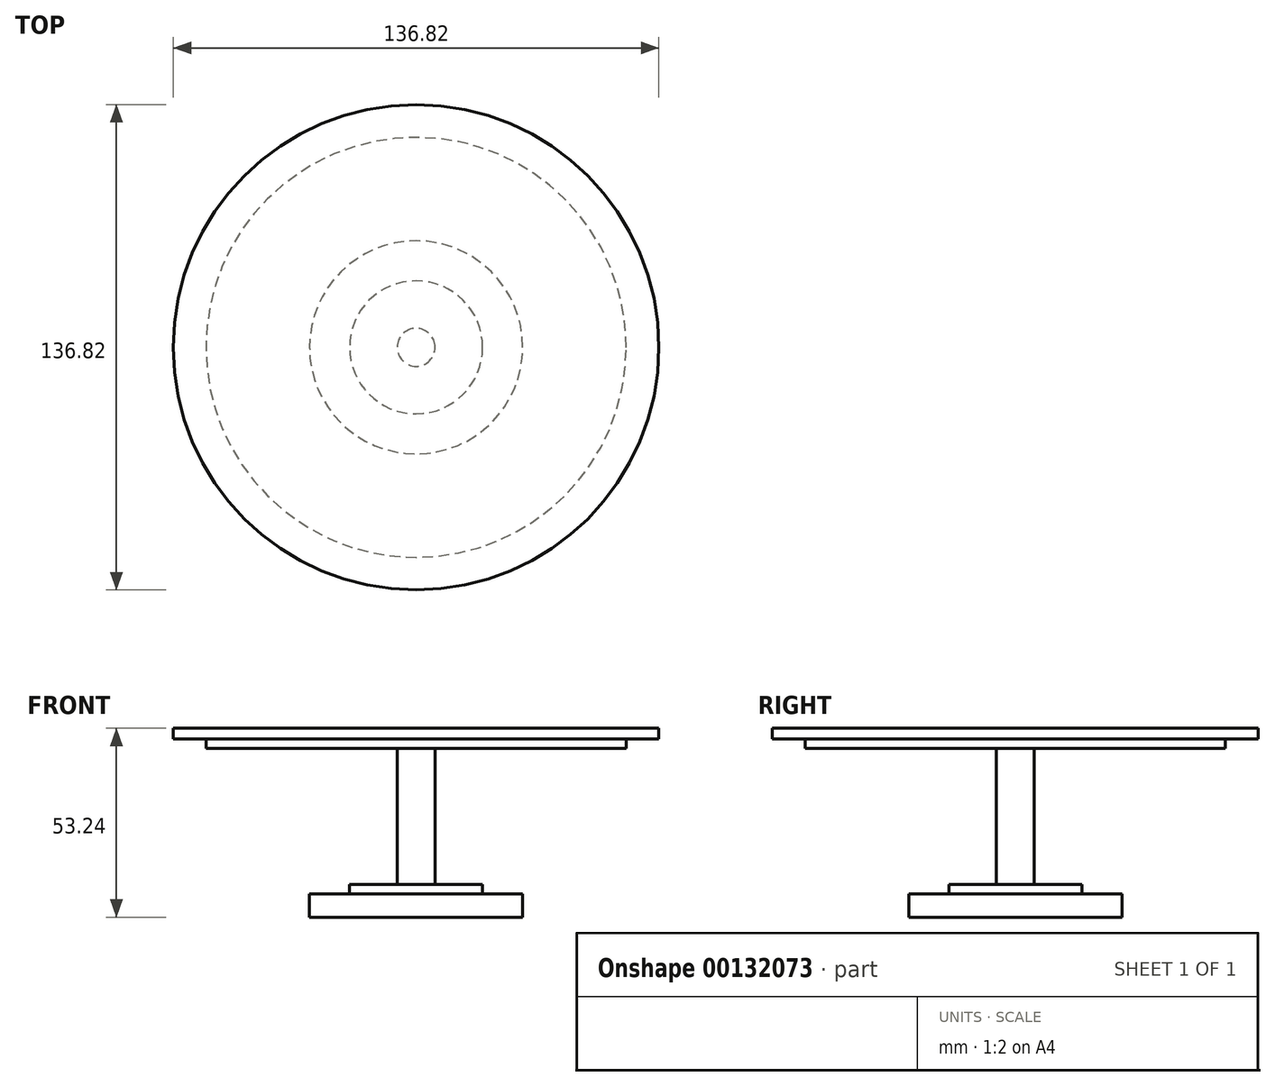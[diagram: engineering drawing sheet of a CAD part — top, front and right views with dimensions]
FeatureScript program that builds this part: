
annotation { "Feature Type Name" : "Feature", "Feature Type Description" : "" }
export const myFeature = defineFeature(function(context is Context, id is Id, definition is map)
    precondition{}
    {
        {
            var Q0;
            Q0=qCreatedBy(makeId("Front.planeOp"),FACE);
            var sketch = newSketch(context, id + "F0", { "sketchPlane" : qUnion([Q0])});
            skLineSegment(sketch, "E0", {"start": v(0, 49.08) * mm, "end": v(-68.41, 49.08) * mm});
            skLineSegment(sketch, "E1", {"start": v(-68.41, 49.08) * mm, "end": v(-68.41, 46.1) * mm});
            skLineSegment(sketch, "E2", {"start": v(-68.41, 46.1) * mm, "end": v(-59.19, 46.1) * mm});
            skLineSegment(sketch, "E3", {"start": v(-59.19, 46.1) * mm, "end": v(-59.19, 43.43) * mm});
            skLineSegment(sketch, "E4", {"start": v(-59.19, 43.43) * mm, "end": v(-5.35, 43.43) * mm});
            skLineSegment(sketch, "E5", {"start": v(-5.35, 43.43) * mm, "end": v(-5.35, 5.06) * mm});
            skLineSegment(sketch, "E6", {"start": v(-5.35, 5.06) * mm, "end": v(-18.74, 5.06) * mm});
            skLineSegment(sketch, "E7", {"start": v(-18.74, 5.06) * mm, "end": v(-18.74, 2.38) * mm});
            skLineSegment(sketch, "E8", {"start": v(-18.74, 2.38) * mm, "end": v(-30.04, 2.38) * mm});
            skLineSegment(sketch, "E9", {"start": v(-30.04, 2.38) * mm, "end": v(-30.04, -4.16) * mm});
            skLineSegment(sketch, "E10", {"start": v(-30.04, -4.16) * mm, "end": v(0, -4.16) * mm});
            skLineSegment(sketch, "E11", {"start": v(0, -4.16) * mm, "end": v(0, 49.08) * mm});
            skSolve(sketch);
        }
        {
            var Q0;
            Q0=makeQuery(id+"F0.imprint","IMPRINT",FACE,{"disambiguationData":[TD([[makeQuery(id+"F0.imprint","IMPRINT",EDGE,{"derivedFrom":sQuery(id+"F0.wireOp",EDGE,"E0")}),1.0]])]});
            var Q1;
            Q1=sQuery(id+"F0.wireOp",EDGE,"E11");
            revolve(context, id + "F1", {"entities" : qUnion([Q0]), "axis" : qUnion([Q1]), "revolveType" : RevolveType.FULL});
        }
    });
